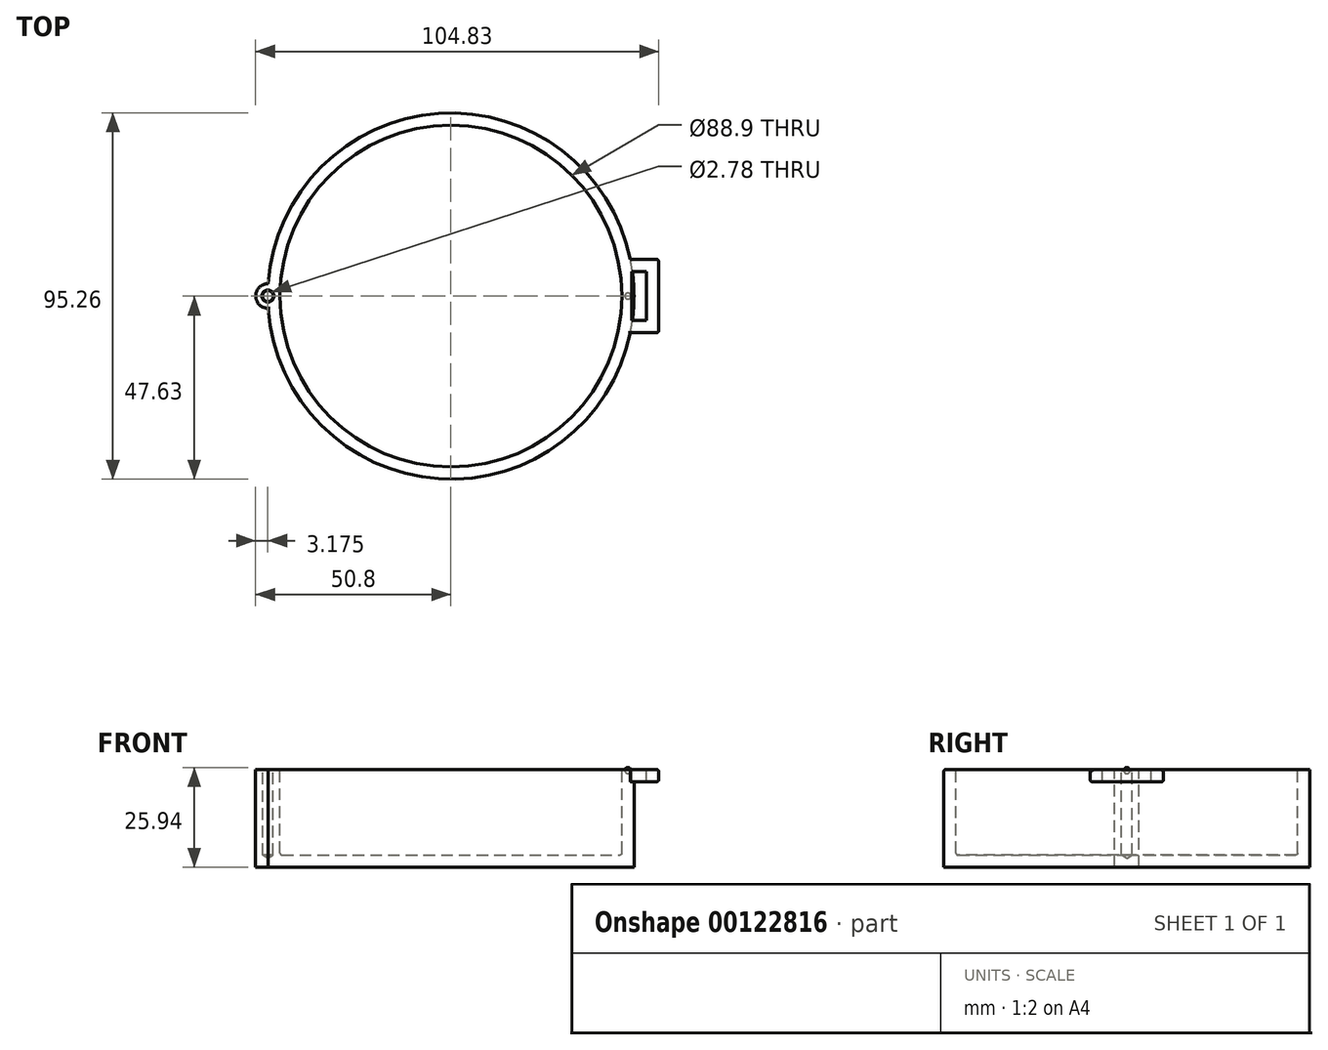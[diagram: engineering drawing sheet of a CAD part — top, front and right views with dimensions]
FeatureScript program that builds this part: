
annotation { "Feature Type Name" : "Feature", "Feature Type Description" : "" }
export const myFeature = defineFeature(function(context is Context, id is Id, definition is map)
    precondition{}
    {
        {
            var Q0;
            Q0=qCreatedBy(makeId("Front.planeOp"),FACE);
            var sketch = newSketch(context, id + "F0", { "sketchPlane" : qUnion([Q0])});
            skLineSegment(sketch, "E0", {"start": v(0, 0) * mm, "end": v(47.62, 0) * mm});
            skLineSegment(sketch, "E1", {"start": v(47.62, 0) * mm, "end": v(47.62, 25.4) * mm});
            skLineSegment(sketch, "E2", {"start": v(47.62, 25.4) * mm, "end": v(44.45, 25.4) * mm});
            skLineSegment(sketch, "E3", {"start": v(44.45, 25.4) * mm, "end": v(44.45, 3.18) * mm});
            skLineSegment(sketch, "E4", {"start": v(44.45, 3.18) * mm, "end": v(0, 3.17) * mm});
            skLineSegment(sketch, "E5", {"start": v(0, 3.17) * mm, "end": v(0, 0) * mm});
            skSolve(sketch);
        }
        {
            var Q0;
            Q0=makeQuery(id+"F0.imprint","IMPRINT",FACE,{"disambiguationData":[TD([[makeQuery(id+"F0.imprint","IMPRINT",EDGE,{"derivedFrom":sQuery(id+"F0.wireOp",EDGE,"E0")}),1.0]])]});
            var Q1;
            Q1=sQuery(id+"F0.wireOp",EDGE,"E5");
            revolve(context, id + "F1", {"entities" : qUnion([Q0]), "axis" : qUnion([Q1]), "revolveType" : RevolveType.FULL});
        }
        {
            var Q0;
            Q0=makeQuery(id+"F1.opRevolve","SWEPT_FACE",FACE,{"disambiguationData":[OSD([sQuery(id+"F0.wireOp",EDGE,"E2")])]});
            var sketch = newSketch(context, id + "F2", { "sketchPlane" : qUnion([Q0])});
            skCircle(sketch, "E6", {"center": v(-47.62, 0) * mm, "radius": 3.17 * mm});
            skSolve(sketch);
        }
        {
            var Q0;
            {var subQ0=sQuery(id+"F2.wireOp",EDGE,"E6");var subQ1=makeQuery(id+"F1.opRevolve","SWEPT_EDGE",EDGE,{"disambiguationData":[OSD([sQuery(id+"F0.wireOp",EDGE,"E1"),sQuery(id+"F0.wireOp",EDGE,"E2")])]});var subQ2=makeQuery(id+"F2.imprint","INTERSECT",VERTEX,{"disambiguationData":[OD(0.0)],"derivedFrom":[subQ1,subQ0]});Q0=makeQuery(id+"F2.imprint","IMPRINT",FACE,{"disambiguationData":[TD([[makeQuery(id+"F2.imprint","IMPRINT",EDGE,{"disambiguationData":[TD([[subQ2,-1.0]])],"derivedFrom":subQ0}),1.0]])]});}
            var Q1;
            Q1=makeQuery(id+"F1.opRevolve","SWEPT_FACE",FACE,{"disambiguationData":[OSD([sQuery(id+"F0.wireOp",EDGE,"E0")])]});
            extrude(context, id + "F3", {"entities" : qUnion([Q0]), "operationType" : NewBodyOperationType.ADD, "endBound" : BoundingType.UP_TO_SURFACE, "oppositeDirection" : true, "endBoundEntityFace" : qUnion([Q1]), "depth" : 25.4 * mm});
        }
        {
            var Q0;
            {var subQ0=sQuery(id+"F0.wireOp",EDGE,"E2");Q0=makeQuery(id+"F3.boolean.opBoolean","MERGE",FACE,{"derivedFrom":[makeQuery(id+"F1.opRevolve","SWEPT_FACE",FACE,{"disambiguationData":[OSD([subQ0])]}),makeQuery(id+"F3.opExtrude","CAP_FACE",FACE,{"disambiguationData":[OSD([sQuery(id+"F0.wireOp",EDGE,"E1"),subQ0,sQuery(id+"F2.wireOp",EDGE,"E6")])],"isStart":true})]});}
            var sketch = newSketch(context, id + "F4", { "sketchPlane" : qUnion([Q0])});
            skPoint(sketch, "E7", {"position": v(-47.62, 0) * mm});
            skSolve(sketch);
        }
        {
            var Q0;
            Q0=sQuery(id+"F4.wireOp",VERTEX,"E7");
            var Q1;
            Q1=makeQuery(id+"F1.opRevolve","SWEPT_BODY",BODY,{"disambiguationData":[OSD([sQuery(id+"F0.wireOp",EDGE,"E0"),sQuery(id+"F0.wireOp",EDGE,"E1"),sQuery(id+"F0.wireOp",EDGE,"E2"),sQuery(id+"F0.wireOp",EDGE,"E3"),sQuery(id+"F0.wireOp",EDGE,"E4"),sQuery(id+"F0.wireOp",EDGE,"E5")])]});
            hole(context, id + "F5", {"style" : HoleStyle.C_SINK, "endStyle" : HoleEndStyle.BLIND, "holeDiameter" : 2.78 * mm, "cSinkDiameter" : 3.17 * mm, "cSinkAngle" : 90 * degree, "holeDepth" : 22.22 * mm, "startFromSketch" : true, "locations" : qUnion([Q0]), "scope" : qUnion([Q1])});
        }
        {
            var Q0;
            Q0=qCreatedBy(makeId("Front.planeOp"),FACE);
            var sketch = newSketch(context, id + "F6", { "sketchPlane" : qUnion([Q0])});
            skCircle(sketch, "E8", {"center": v(46.04, 25.15) * mm, "radius": 0.8 * mm});
            skLineSegment(sketch, "E9", {"start": v(45.24, 25.15) * mm, "end": v(46.83, 25.15) * mm});
            skSolve(sketch);
        }
        {
            var Q0;
            {var subQ0=sQuery(id+"F6.wireOp",EDGE,"E9");Q0=makeQuery(id+"F6.imprint","IMPRINT",FACE,{"disambiguationData":[TD([[makeQuery(id+"F6.imprint","IMPRINT",EDGE,{"derivedFrom":subQ0}),1.0]])]});}
            var Q1;
            Q1=sQuery(id+"F6.wireOp",EDGE,"E9");
            var Q2;
            Q2=sQuery(id+"F6.wireOp",EDGE,"E9");
            revolve(context, id + "F7", {"entities" : qUnion([Q0]), "surfaceEntities" : qUnion([Q1]), "axis" : qUnion([Q2]), "revolveType" : RevolveType.FULL});
        }
        {
            var Q0;
            {var subQ0=sQuery(id+"F0.wireOp",EDGE,"E2");Q0=makeQuery(id+"F3.boolean.opBoolean","MERGE",FACE,{"derivedFrom":[makeQuery(id+"F1.opRevolve","SWEPT_FACE",FACE,{"disambiguationData":[OSD([subQ0])]}),makeQuery(id+"F3.opExtrude","CAP_FACE",FACE,{"disambiguationData":[OSD([sQuery(id+"F0.wireOp",EDGE,"E1"),subQ0,sQuery(id+"F2.wireOp",EDGE,"E6")])],"isStart":true})]});}
            var sketch = newSketch(context, id + "F8", { "sketchPlane" : qUnion([Q0])});
            skLineSegment(sketch, "E10.bottom", {"start": v(54.03, 9.52) * mm, "end": v(41.33, 9.52) * mm});
            skLineSegment(sketch, "E10.top", {"start": v(54.03, -9.53) * mm, "end": v(41.33, -9.53) * mm});
            skLineSegment(sketch, "E10.left", {"start": v(54.03, 9.52) * mm, "end": v(54.03, -9.53) * mm});
            skLineSegment(sketch, "E10.right", {"start": v(41.33, 9.52) * mm, "end": v(41.33, -9.53) * mm});
            skPoint(sketch, "E10.middle", {"position": v(47.68, 0) * mm});
            skLineSegment(sketch, "E11.bottom", {"start": v(50.85, 6.35) * mm, "end": v(47.04, 6.35) * mm});
            skLineSegment(sketch, "E11.top", {"start": v(50.85, -6.35) * mm, "end": v(47.04, -6.35) * mm});
            skLineSegment(sketch, "E11.left", {"start": v(50.85, 6.35) * mm, "end": v(50.85, -6.35) * mm});
            skLineSegment(sketch, "E12", {"start": v(47.04, 6.35) * mm, "end": v(47.04, -6.35) * mm});
            skPoint(sketch, "E13.orphan", {"position": v(44.5, 6.35) * mm});
            skPoint(sketch, "E14.orphan", {"position": v(44.5, -6.35) * mm});
            skLineSegment(sketch, "E15", {"start": v(0, 0) * mm, "end": v(47.62, 0) * mm, "construction": true});
            skSolve(sketch);
        }
        {
            var Q0;
            {var subQ0=sQuery(id+"F8.wireOp",EDGE,"E10.left");Q0=makeQuery(id+"F8.imprint","IMPRINT",FACE,{"disambiguationData":[TD([[makeQuery(id+"F8.imprint","IMPRINT",EDGE,{"derivedFrom":subQ0}),-1.0]])]});}
            extrude(context, id + "F9", {"entities" : qUnion([Q0]), "operationType" : NewBodyOperationType.ADD, "oppositeDirection" : true, "depth" : 3.17 * mm});
        }
        {
            var Q0;
            {var subQ0=sQuery(id+"F8.wireOp",EDGE,"E12");Q0=makeQuery(id+"F8.imprint","IMPRINT",FACE,{"disambiguationData":[TD([[makeQuery(id+"F8.imprint","IMPRINT",EDGE,{"derivedFrom":subQ0}),1.0]])]});}
            extrude(context, id + "F10", {"entities" : qUnion([Q0]), "operationType" : NewBodyOperationType.REMOVE, "oppositeDirection" : true, "depth" : 3.17 * mm});
        }
        {
            var Q0;
            Q0=makeQuery(id+"F9.opExtrude","SWEPT_EDGE",EDGE,{"disambiguationData":[OSD([sQuery(id+"F0.wireOp",EDGE,"E1"),sQuery(id+"F0.wireOp",EDGE,"E2"),sQuery(id+"F8.wireOp",EDGE,"E10.top")])]});
            var Q1;
            Q1=makeQuery(id+"F9.opExtrude","SWEPT_EDGE",EDGE,{"disambiguationData":[OSD([sQuery(id+"F8.wireOp",EDGE,"E10.top"),sQuery(id+"F8.wireOp",EDGE,"E10.left")])]});
            var Q2;
            Q2=makeQuery(id+"F9.opExtrude","SWEPT_EDGE",EDGE,{"disambiguationData":[OSD([sQuery(id+"F8.wireOp",EDGE,"E10.bottom"),sQuery(id+"F8.wireOp",EDGE,"E10.left")])]});
            var Q3;
            Q3=makeQuery(id+"F9.opExtrude","SWEPT_EDGE",EDGE,{"disambiguationData":[OSD([sQuery(id+"F0.wireOp",EDGE,"E1"),sQuery(id+"F0.wireOp",EDGE,"E2"),sQuery(id+"F8.wireOp",EDGE,"E10.bottom")])]});
            var Q4;
            {var subQ0=sQuery(id+"F2.wireOp",EDGE,"E6");var subQ1=sQuery(id+"F0.wireOp",EDGE,"E2");var subQ2=sQuery(id+"F0.wireOp",EDGE,"E1");Q4=makeQuery(id+"F3.opExtrude","SWEPT_EDGE",EDGE,{"disambiguationData":[OSD([subQ2,subQ1,subQ0]),TDD([makeQuery(id+"F2.imprint","INTERSECT",VERTEX,{"disambiguationData":[OD(0.0)],"derivedFrom":[makeQuery(id+"F1.opRevolve","SWEPT_EDGE",EDGE,{"disambiguationData":[OSD([subQ2,subQ1])]}),subQ0]})])]});}
            var Q5;
            {var subQ0=sQuery(id+"F2.wireOp",EDGE,"E6");var subQ1=sQuery(id+"F0.wireOp",EDGE,"E2");var subQ2=sQuery(id+"F0.wireOp",EDGE,"E1");Q5=makeQuery(id+"F3.opExtrude","SWEPT_EDGE",EDGE,{"disambiguationData":[OSD([subQ2,subQ1,subQ0]),TDD([makeQuery(id+"F2.imprint","INTERSECT",VERTEX,{"disambiguationData":[OD(1.0)],"derivedFrom":[makeQuery(id+"F1.opRevolve","SWEPT_EDGE",EDGE,{"disambiguationData":[OSD([subQ2,subQ1])]}),subQ0]})])]});}
            var Q6;
            Q6=makeQuery(id+"F1.opRevolve","SWEPT_EDGE",EDGE,{"disambiguationData":[OSD([sQuery(id+"F0.wireOp",EDGE,"E3"),sQuery(id+"F0.wireOp",EDGE,"E4")])]});
            var Q7;
            Q7=makeQuery(id+"F1.opRevolve","SWEPT_EDGE",EDGE,{"disambiguationData":[OSD([sQuery(id+"F0.wireOp",EDGE,"E2"),sQuery(id+"F0.wireOp",EDGE,"E3")])]});
            var Q8;
            {var subQ0=sQuery(id+"F0.wireOp",EDGE,"E2");var subQ2=sQuery(id+"F0.wireOp",EDGE,"E1");var subQ3=sQuery(id+"F8.wireOp",EDGE,"E10.top");Q8=makeQuery(id+"F9.boolean.opBoolean","SPLIT",EDGE,{"disambiguationData":[TD([makeQuery(id+"F9.opExtrude","SWEPT_FACE",FACE,{"disambiguationData":[OSD([subQ3])]})])],"derivedFrom":makeQuery(id+"F1.opRevolve","SWEPT_EDGE",EDGE,{"disambiguationData":[OSD([subQ2,subQ0])]})});}
            var Q9;
            Q9=makeQuery(id+"F9.opExtrude","CAP_EDGE",EDGE,{"disambiguationData":[OSD([sQuery(id+"F8.wireOp",EDGE,"E10.bottom")])],"isStart":false});
            var Q10;
            Q10=makeQuery(id+"F9.opExtrude","CAP_EDGE",EDGE,{"disambiguationData":[OSD([sQuery(id+"F8.wireOp",EDGE,"E10.left")])],"isStart":false});
            var Q11;
            Q11=makeQuery(id+"F9.opExtrude","CAP_EDGE",EDGE,{"disambiguationData":[OSD([sQuery(id+"F8.wireOp",EDGE,"E10.top")])],"isStart":false});
            var Q12;
            Q12=makeQuery(id+"F9.opExtrude","CAP_EDGE",EDGE,{"disambiguationData":[OSD([sQuery(id+"F8.wireOp",EDGE,"E10.left")])],"isStart":true});
            fillet(context, id + "F11", {"entities" : qUnion([Q0, Q1, Q2, Q3, Q4, Q5, Q6, Q7, Q8, Q9, Q10, Q11, Q12]), "radius" : 0.5 * mm, "tangentPropagation" : true, "allowEdgeOverflow" : false});
        }
    });
